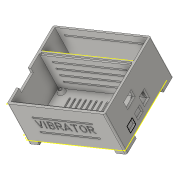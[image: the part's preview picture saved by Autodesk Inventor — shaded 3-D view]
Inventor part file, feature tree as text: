
AUTODESK INVENTOR PART (.ipt)
format: ipt  version: 2016 (Build 200138000, 138)  size: 761,344 bytes
history: native  units: mm
features: sketch x53, extrude x47, fillet x5
ambient origin geometry x8: Origin, YZ Plane, XZ Plane, XY Plane, X Axis, Y Axis, Z Axis, Center Point
bodies: Volumenkörper1 (feature_tree)
feature tree (105):
  extrude  "Extrusion1"  Depth=88.0mm
  extrude  "Extrusion2"  Depth=104.0mm
  sketch  "Skizze3"  dims[d5=58.0mm d6=47.0mm d7=0.0mm]
  extrude  "Extrusion5"  Depth=47.0mm TaperAngle=0.0deg
  extrude  "Extrusion6"  Depth=4.0mm
  sketch  "Skizze8"  dims[d22=9.0mm d23=4.0mm d24=-5.235988mm]
  extrude  "Extrusion7"  Depth=4.0mm
  extrude  "Extrusion8"  Depth=4.0mm
  extrude  "Extrusion10"  Depth=4.0mm
  sketch  "Skizze13"  dims[d38=2.5mm d39=10.0mm d40=0.0mm]
  sketch  "Skizze14"  dims[d41=2.5mm d42=10.0mm d43=0.0mm]
  extrude  "Extrusion11"  Depth=2.0mm TaperAngle=0.0deg
  extrude  "Extrusion12"  Depth=10.0mm TaperAngle=0.0deg
  extrude  "Extrusion13"  Depth=10.0mm TaperAngle=0.0deg
  extrude  "Extrusion14"  Depth=10.0mm TaperAngle=0.0deg
  extrude  "Extrusion25"  Depth=10.0mm TaperAngle=0.0deg
  fillet  "Rundung1"  Radius=1.0mm
  fillet  "Rundung3"  Radius=2.0mm
  extrude  "Extrusion26"  Depth=12.0mm
  extrude  "Extrusion27"  Depth=12.0mm
  sketch  "Skizze32"  dims[d105=5.0mm d106=0.0mm d107=6.0mm]
  extrude  "Extrusion28"  Depth=12.0mm
  extrude  "Extrusion29"  Depth=12.0mm
  extrude  "Extrusion30"  Depth=6.0mm
  extrude  "Extrusion31"  Depth=6.0mm
  extrude  "Extrusion32"  Depth=6.0mm
  extrude  "Extrusion33"  Depth=6.0mm
  extrude  "Extrusion34"  Depth=66.0mm
  extrude  "Extrusion35"  Depth=5.0mm TaperAngle=0.0deg
  extrude  "Extrusion38"  Depth=5.0mm TaperAngle=0.0deg
  extrude  "Extrusion39"  Depth=10.0mm TaperAngle=0.0deg
  extrude  "Extrusion40"  Depth=10.0mm TaperAngle=0.0deg
  extrude  "Extrusion41"  Depth=10.0mm TaperAngle=0.0deg
  extrude  "Extrusion44"  Depth=10.0mm TaperAngle=0.0deg
  extrude  "Extrusion45"  Depth=48.0mm TaperAngle=0.0deg
  fillet  "Rundung5"  Radius=2.0mm
  fillet  "Rundung6"  Radius=2.0mm
  extrude  "Extrusion48"  Depth=10.0mm TaperAngle=0.0deg
  extrude  "Extrusion49"  Depth=10.0mm TaperAngle=0.0deg
  extrude  "Extrusion50"  Depth=10.0mm TaperAngle=0.0deg
  extrude  "Extrusion51"  Depth=40.0mm
  sketch  "Skizze57"  dims[d203=10.0mm d204=0.0mm d205=1.0mm d206=0.0mm d207=1.0mm d208=0.0mm]
  extrude  "Extrusion52"  Depth=5.0mm TaperAngle=0.0deg
  extrude  "Extrusion53"  Depth=2.0mm
  extrude  "Extrusion54"  Depth=5.0mm TaperAngle=0.0deg
  extrude  "Extrusion55"  Depth=110.0mm
  extrude  "Extrusion56"  Depth=2.0mm TaperAngle=0.0deg
  extrude  "Extrusion57"  Depth=1.0mm TaperAngle=0.0deg
  fillet  "Rundung7"  Radius=1.0mm
  extrude  "Extrusion58"  Depth=5.0mm TaperAngle=0.0deg
  extrude  "Extrusion59"  [1 undecoded]
  extrude  "Extrusion60"  [1 undecoded]
  extrude  "Extrusion61"  [1 undecoded]
  extrude  "Extrusion63"  [1 undecoded]
  extrude  "Extrusion65"  [1 undecoded]
  sketch  "Skizze70"
  extrude  "Extrusion66"  [1 undecoded]
  extrude  "Extrusion67"  [1 undecoded]
  extrude  "Extrusion68"  [1 undecoded]
  sketch  "Skizze1"  dims[d0=110.0mm d1=88.0mm]
  sketch  "Skizze2"  dims[d2=50.0mm d3=0.0mm d4=104.0mm]
  sketch  "Skizze6"  dims[d16=9.0mm d17=4.0mm d18=-5.235988mm]
  sketch  "Skizze7"  dims[d19=9.0mm d20=4.0mm d21=-5.235988mm]
  sketch  "Skizze9"  dims[d25=9.0mm d26=4.0mm d27=-5.235988mm]
  sketch  "Skizze10"  dims[d32=2.0mm d33=2.0mm d34=0.0mm]
  sketch  "Skizze12"  dims[d35=2.5mm d36=10.0mm d37=0.0mm]
  sketch  "Skizze15"  dims[d44=2.5mm d45=10.0mm d46=0.0mm d83=1.0mm d84=0.0mm d85=2.0mm]
  sketch  "Skizze16"  dims[d87=2.0mm d89=12.0mm]
  sketch  "Skizze17"  dims[d90=5.0mm d91=-3.490659mm d92=12.0mm]
  sketch  "Skizze18"  dims[d93=5.0mm d94=-3.490659mm d95=12.0mm]
  sketch  "Skizze29"  dims[d96=5.0mm d97=-3.490659mm d98=12.0mm]
  sketch  "Skizze30"  dims[d99=5.0mm d100=-3.490659mm d101=6.0mm]
  sketch  "Skizze31"  dims[d102=5.0mm d103=0.0mm d104=6.0mm]
  sketch  "Skizze33"  dims[d108=5.0mm d109=0.0mm d110=6.0mm]
  sketch  "Skizze34"  dims[d111=5.0mm d112=0.0mm d113=66.0mm]
  sketch  "Skizze35"  dims[d114=2.0mm d115=5.0mm d116=0.0mm]
  sketch  "Skizze36"  dims[d117=2.0mm d118=5.0mm d119=0.0mm]
  sketch  "Skizze37"  dims[d126=3.5mm d127=10.0mm d128=0.0mm]
  sketch  "Skizze38"  dims[d129=3.5mm d130=10.0mm d131=0.0mm]
  sketch  "Skizze39"  dims[d132=3.5mm d133=10.0mm d134=0.0mm]
  sketch  "Skizze40"  dims[d135=3.5mm d136=10.0mm d137=0.0mm]
  sketch  "Skizze43"  dims[d142=10.0mm d143=0.0mm d144=48.0mm d145=0.0mm d146=2.0mm d147=2.0mm]
  sketch  "Skizze44"  dims[d154=2.0mm d155=0.0mm d156=10.0mm d157=0.0mm]
  sketch  "Skizze45"  dims[d158=10.0mm d159=0.0mm d160=10.0mm d161=0.0mm]
  sketch  "Skizze46"  dims[d162=10.0mm d163=0.0mm d164=10.0mm d165=0.0mm]
  sketch  "Skizze49"  dims[d166=10.0mm d167=0.0mm d168=40.0mm d170=9.0mm d171=10.0mm d173=10.0mm]
  sketch  "Skizze50"  dims[d175=10.0mm d176=0.0mm d177=5.0mm d178=0.0mm]
  sketch  "Skizze53"  dims[d179=5.0mm d180=0.0mm d181=2.0mm]
  sketch  "Skizze54"  dims[d182=5.0mm d183=0.0mm d184=5.0mm d185=0.0mm]
  sketch  "Skizze55"  dims[d186=5.0mm d187=0.0mm d188=110.0mm d190=6.0mm d191=10.0mm d193=10.0mm]
  sketch  "Skizze56"  dims[d195=10.0mm d196=0.0mm d199=2.0mm d200=0.0mm]
  sketch  "Skizze58"  dims[d209=2.0mm d210=5.0mm d211=0.0mm]
  sketch  "Skizze59"
  sketch  "Skizze60"
  sketch  "Skizze61"
  sketch  "Skizze62"
  sketch  "Skizze63"
  sketch  "Skizze64"
  sketch  "Skizze65"
  sketch  "Skizze66"
  sketch  "Skizze68"
  sketch  "Skizze69"
  sketch  "Skizze71"
  sketch  "Skizze72"
  sketch  "Skizze73"
note: 8 required parameter values undecoded (feature->parameter linkage not recoverable at this tier; creation-order binding heuristic only, values carry confidence <= 0.55)
